# Revit family: IS_Connect_E8233_BIM_DE
name_source: partatom
category: Plumbing Fixtures
revit_build: Autodesk Revit MEP 2016 (Build: 20161004_0715(x64)
units: mm (PartAtom-declared; Revit-internal decimal feet)

## family parameters
Always vertical = No
Cut with Voids When Loaded = No
OmniClass Number = 23.45.05.21.11.11
OmniClass Title = Water Operated Water Closets
Part Type = Normal
Room Calculation Point = No
Round Connector Dimension = Use Diameter
Shared = No
Work Plane-Based = No

## types (2) — shared parameters
Accessories = www.idealstandard.de\ersatzteile
AreaUnits = millimeters
AssetType = Fixed
BIMobject category = Toilets
BOSUseNativeGeometries = 1
Brand = Ideal Standard
Brand url = http://www.idealstandard.co.uk
CodePerformance = DIN EN 997, CL1-6-VRII, DIN EN 33
ConnectionType = Plumbing
CurrencyUnit = €
CurrentRevision = 1
Date of publishing = 2017_11_20
DurationUnit = year
Edition number = 1
ExpectedLife = 25
Features = CONNECT close couple floor standing bowl 360x660mm, wash-down
IFC Classification = Sanitary Terminal
IfcExportAs = IfcSanitaryTerminalType
IfcExportType = TOILETPANS
Installation instructions = http://www.idealstandard.de
InstallationInstructions = www.idealstandard.de\produkte
LinearUnits = millimeters
Manufacturer name = Ideal Standard
ManufacturerURL = www.idealstandard.com
Material = Vitreous china
Material main = Ceramics
NBS Reference Code = 35-93-94
NBS Reference Description = Wc Pans
Nominal height = 775
Nominal width = 360
NominalDepth = 660 mm
NominalHeight = 400 mm
NominalLength = 660 mm
NominalWidth = 361 mm
OmniClass Code = 23-31 19 00
OmniClass Description = Toilets
PanMaterial = Vitreous china
Product Guid = 50a43852-29dd-48ee-b55c-05648610147a
Product SKU = E8233
Product certification = DIN EN 997, CL1-6-VRII, DIN EN 33
Product data url = https://bimobject.com
Product family = CONNECT
Product group = Bowl
Product name = CONNECT close couple floor standing bowl 360x660mm, wash-down
Product url = http://www.idealstandard.de
ProductInformation = www.idealstandard.de/produkte
QR code = http://bimobject.com
Shape = Sculptured
Size = 400 x 660 x 361mm
Space = Internal
SpareParts = www.idealstandard.de/ersatzteile
Technical description = http://www.idealstandard.de
ToiletType = WashDown
URL = http://www.idealstandard.de
Uniclass 1.4 Code = L7216
Uniclass 1.4 Description = Toilets
Uniclass 2.0 Code = PR-35-93-97
Uniclass 2.0 Description = Wc Suites
Uniclass 2015 Code = Pr_40_20_93_97
Uniclass 2015 Name = WC suites
Uniclass2015Code = Pr_40_20_93_97
Uniclass2015Title = WC suites
Uniclass2015Version = Products v1.1
Version = 1
VolumeUnits = Litres
Weight Net (Kg) = 26.03
zero-valued in all types: Cost, SpilloverLevel

## per-type parameters (varying)
| type | BIMObjectName | BarCode | Color | Description | EAN code | Finish | MainColor | Model | ModelNumber | ModelReference | Name | NettWeight | PanColor |
| E823301 - CONNECT close couple floor standing bowl 360x660mm, wash-down | ISI_IdealStandard_WcPans_Connect_E823301 | 5017830448686 | White | E823301 CONNECT close couple floor standing bowl 360x660mm, wash-down | 5017830448686 | White | White | E823301 | E823301 | E823301 CONNECT close couple floor standing bowl 360x660mm, wash-down | WcPans_Connect_E823301_IdealStandard | 26,03 kg | White |
| E8233MA - CONNECT close couple floor standing bowl 360x660mm, wash-down | ISI_IdealStandard_WcPans_Connect_E8233MA | 5017830448976 | WHITE IP | E8233MA CONNECT close couple floor standing bowl 360x660mm, wash-down | 5017830448976 | WHITE IP | WHITE IP | E8233MA | E8233MA | E8233MA CONNECT close couple floor standing bowl 360x660mm, wash-down | WcPans_Connect_E8233MA_IdealStandard | 24 kg | WHITE IP |

## geometry (parser evidence)
native form markers: Blend x2, Sweep x3
no freeform markers — native parametric forms only
